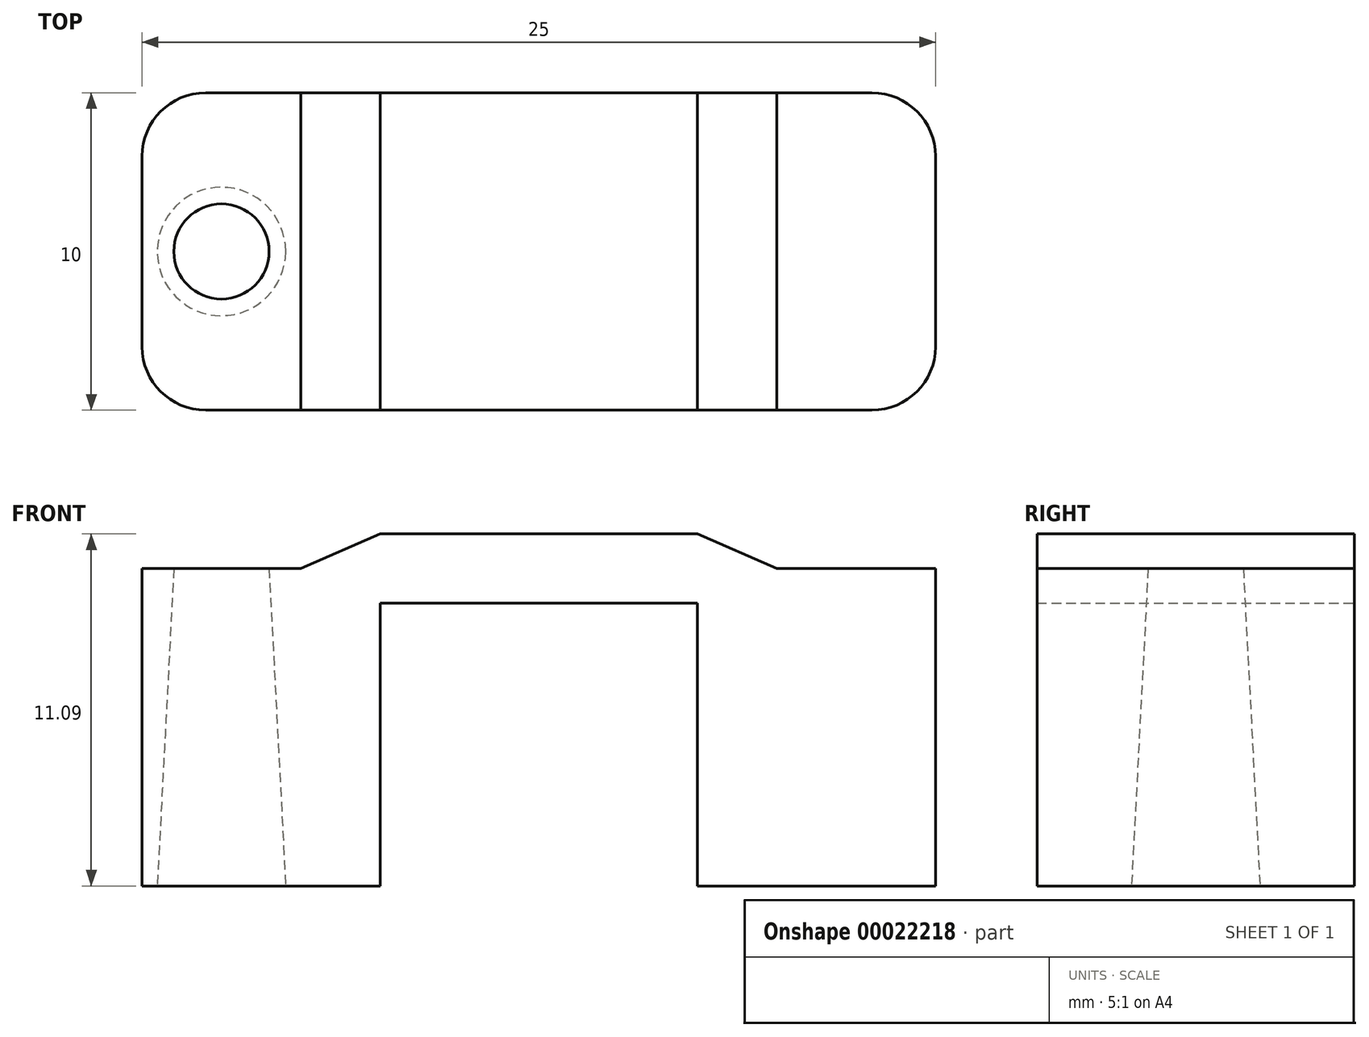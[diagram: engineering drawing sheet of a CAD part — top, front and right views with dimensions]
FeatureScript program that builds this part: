
annotation { "Feature Type Name" : "Feature", "Feature Type Description" : "" }
export const myFeature = defineFeature(function(context is Context, id is Id, definition is map)
    precondition{}
    {
        {
            var Q0;
            Q0=qCreatedBy(makeId("Front.planeOp"),FACE);
            var sketch = newSketch(context, id + "F0", { "sketchPlane" : qUnion([Q0])});
            skLineSegment(sketch, "E0.rect.bottom", {"start": v(12.5, -5) * mm, "end": v(-12.5, -5) * mm});
            skLineSegment(sketch, "E0.rect.top", {"start": v(12.5, 5) * mm, "end": v(7.5, 5) * mm});
            skLineSegment(sketch, "E0.rect.left", {"start": v(12.5, -5) * mm, "end": v(12.5, 5) * mm});
            skLineSegment(sketch, "E0.rect.right", {"start": v(-12.5, -5) * mm, "end": v(-12.5, 5) * mm});
            skPoint(sketch, "E0.rect.middle", {"position": v(0, 0) * mm});
            skLineSegment(sketch, "E1.rect.bottom", {"start": v(5, -5) * mm, "end": v(-5, -5) * mm});
            skLineSegment(sketch, "E1.rect.left", {"start": v(5, -5) * mm, "end": v(5, 3.9) * mm});
            skLineSegment(sketch, "E1.rect.right", {"start": v(-5, -5) * mm, "end": v(-5, 3.9) * mm});
            skLineSegment(sketch, "E2.rect.bottom", {"start": v(5, 6.1) * mm, "end": v(-5, 6.1) * mm});
            skLineSegment(sketch, "E2.rect.top", {"start": v(5, 3.9) * mm, "end": v(-5, 3.9) * mm});
            skPoint(sketch, "E2.rect.middle", {"position": v(0, 5) * mm});
            skLineSegment(sketch, "E3.trimOffspring", {"start": v(-7.5, 5) * mm, "end": v(-12.5, 5) * mm});
            skLineSegment(sketch, "E4", {"start": v(-7.5, 5) * mm, "end": v(-5, 6.1) * mm});
            skLineSegment(sketch, "E5", {"start": v(7.5, 5) * mm, "end": v(5, 6.1) * mm});
            skPoint(sketch, "E2.rect.right.end.orphan", {"position": v(-5, 5) * mm});
            skPoint(sketch, "E6.orphan", {"position": v(5, 5) * mm});
            skSolve(sketch);
        }
        {
            var Q0;
            Q0=makeQuery(id+"F0.imprint","IMPRINT",FACE,{"disambiguationData":[TD([[makeQuery(id+"F0.imprint","IMPRINT",EDGE,{"derivedFrom":sQuery(id+"F0.wireOp",EDGE,"E0.rect.top")}),1.0]])]});
            extrude(context, id + "F1", {"entities" : qUnion([Q0]), "depth" : 10 * mm});
        }
        {
            var Q0;
            Q0=makeQuery(id+"F1.opExtrude","SWEPT_FACE",FACE,{"disambiguationData":[OSD([sQuery(id+"F0.wireOp",EDGE,"E3.trimOffspring")])]});
            var sketch = newSketch(context, id + "F2", { "sketchPlane" : qUnion([Q0])});
            skLineSegment(sketch, "E7", {"start": v(-10, 0) * mm, "end": v(-10, -10) * mm, "construction": true});
            skLineSegment(sketch, "E8", {"start": v(-12.5, -5) * mm, "end": v(-7.5, -5) * mm, "construction": true});
            skCircle(sketch, "E9", {"center": v(-10, -5) * mm, "radius": 1.5 * mm});
            skCircle(sketch, "E10.MirrorC", {"center": v(10, -5) * mm, "radius": 1.5 * mm});
            skSolve(sketch);
        }
        {
            var Q0;
            Q0=makeQuery(id+"F2.imprint","IMPRINT",FACE,{"disambiguationData":[TD([[makeQuery(id+"F2.imprint","IMPRINT",EDGE,{"derivedFrom":sQuery(id+"F2.wireOp",EDGE,"E9")}),1.0]])]});
            var Q1;
            Q1=makeQuery(id+"F2.imprint","IMPRINT",FACE,{"disambiguationData":[TD([[makeQuery(id+"F2.imprint","IMPRINT",EDGE,{"derivedFrom":sQuery(id+"F2.wireOp",EDGE,"E10.MirrorC")}),-1.0]])]});
            extrude(context, id + "F3", {"entities" : qUnion([Q0, Q1]), "operationType" : NewBodyOperationType.REMOVE, "oppositeDirection" : true, "depth" : 25 * mm, "hasDraft" : true, "draftAngle" : 3 * degree});
        }
        {
            var Q0;
            Q0=makeQuery(id+"F1.opExtrude","CAP_EDGE",EDGE,{"disambiguationData":[OSD([sQuery(id+"F0.wireOp",EDGE,"E0.rect.right")])],"isStart":false});
            var Q1;
            Q1=makeQuery(id+"F1.opExtrude","CAP_EDGE",EDGE,{"disambiguationData":[OSD([sQuery(id+"F0.wireOp",EDGE,"E0.rect.right")])],"isStart":true});
            var Q2;
            Q2=makeQuery(id+"F1.opExtrude","CAP_EDGE",EDGE,{"disambiguationData":[OSD([sQuery(id+"F0.wireOp",EDGE,"E0.rect.left")])],"isStart":false});
            var Q3;
            Q3=makeQuery(id+"F1.opExtrude","CAP_EDGE",EDGE,{"disambiguationData":[OSD([sQuery(id+"F0.wireOp",EDGE,"E0.rect.left")])],"isStart":true});
            fillet(context, id + "F4", {"entities" : qUnion([Q0, Q1, Q2, Q3]), "radius" : 2 * mm, "tangentPropagation" : true, "allowEdgeOverflow" : false});
        }
    });
